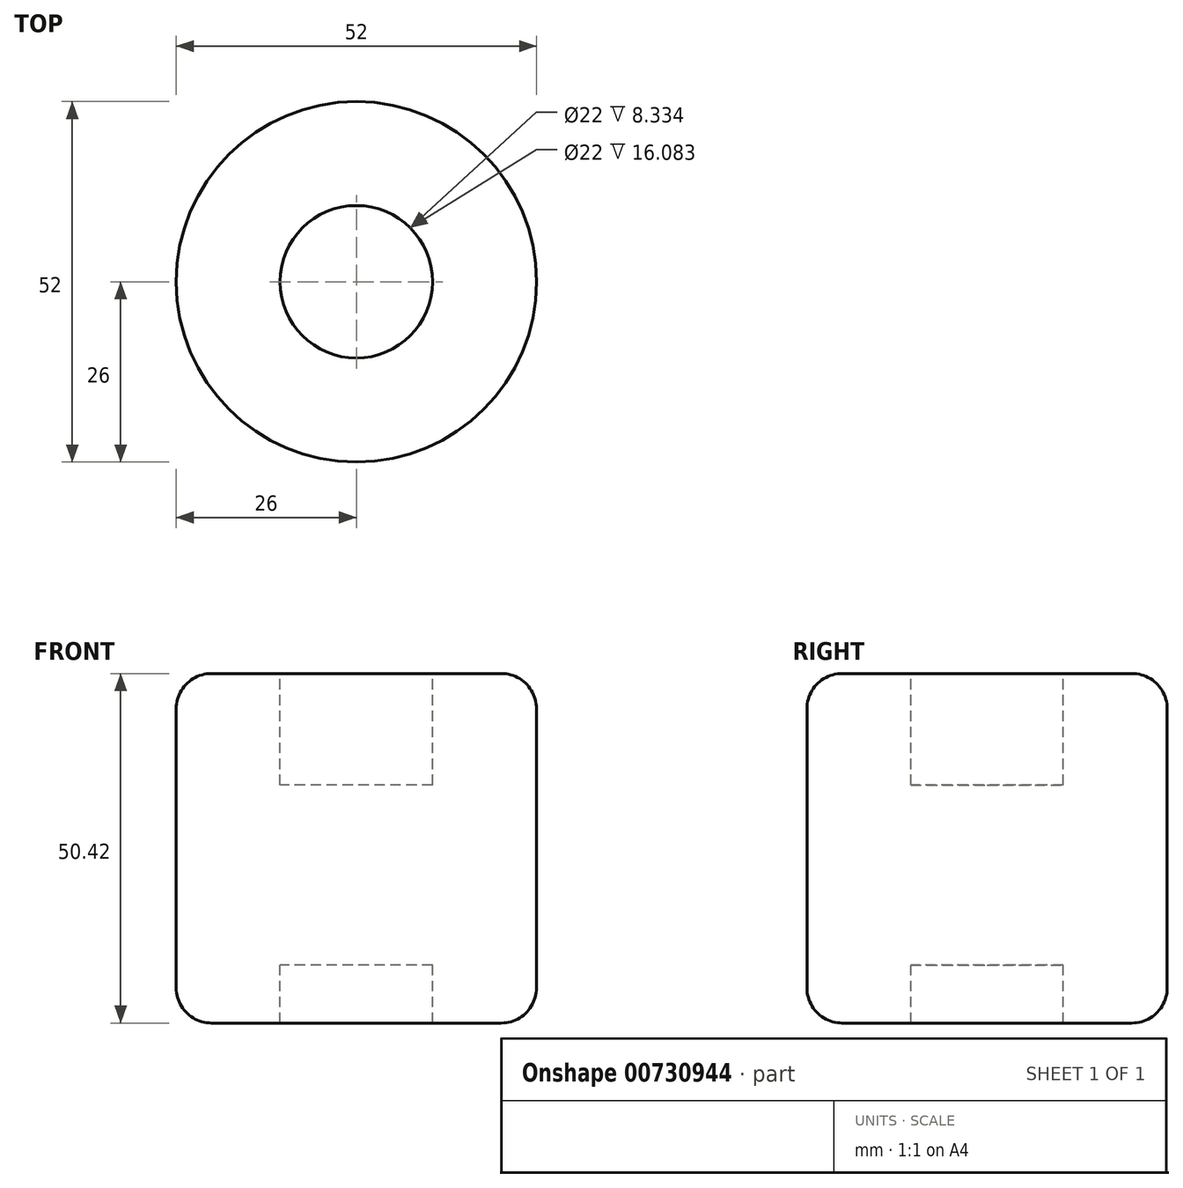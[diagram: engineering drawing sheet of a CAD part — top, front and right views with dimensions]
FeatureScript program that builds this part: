
annotation { "Feature Type Name" : "Feature", "Feature Type Description" : "" }
export const myFeature = defineFeature(function(context is Context, id is Id, definition is map)
    precondition{}
    {
        {
            var Q0;
            Q0=qCreatedBy(makeId("Front.planeOp"),FACE);
            var sketch = newSketch(context, id + "F0", { "sketchPlane" : qUnion([Q0])});
            skLineSegment(sketch, "E0", {"start": v(0, 8.33) * mm, "end": v(11, 8.33) * mm});
            skLineSegment(sketch, "E1", {"start": v(11, 8.33) * mm, "end": v(11, 0) * mm});
            skLineSegment(sketch, "E2", {"start": v(11, 0) * mm, "end": v(26, 0) * mm});
            skLineSegment(sketch, "E3", {"start": v(26, 0) * mm, "end": v(26, 50.42) * mm});
            skLineSegment(sketch, "E4", {"start": v(26, 50.42) * mm, "end": v(11, 50.42) * mm});
            skLineSegment(sketch, "E5", {"start": v(11, 50.42) * mm, "end": v(11, 34.33) * mm});
            skLineSegment(sketch, "E6", {"start": v(11, 34.33) * mm, "end": v(0, 34.33) * mm});
            skLineSegment(sketch, "E7", {"start": v(0, 34.33) * mm, "end": v(0, 8.33) * mm});
            skSolve(sketch);
        }
        {
            var Q0;
            Q0=makeQuery(id+"F0.imprint","IMPRINT",FACE,{"disambiguationData":[TD([[makeQuery(id+"F0.imprint","IMPRINT",EDGE,{"derivedFrom":sQuery(id+"F0.wireOp",EDGE,"E0")}),1.0]])]});
            var Q1;
            Q1=sQuery(id+"F0.wireOp",EDGE,"E7");
            revolve(context, id + "F1", {"surfaceOperationType" : NewSurfaceOperationType.NEW, "entities" : qUnion([Q0]), "axis" : qUnion([Q1]), "revolveType" : RevolveType.FULL});
        }
        {
            var Q0;
            Q0=makeQuery(id+"F1.opRevolve","SWEPT_EDGE",EDGE,{"disambiguationData":[OSD([sQuery(id+"F0.wireOp",EDGE,"E3"),sQuery(id+"F0.wireOp",EDGE,"E4")])]});
            var Q1;
            Q1=makeQuery(id+"F1.opRevolve","SWEPT_EDGE",EDGE,{"disambiguationData":[OSD([sQuery(id+"F0.wireOp",EDGE,"E2"),sQuery(id+"F0.wireOp",EDGE,"E3")])]});
            fillet(context, id + "F2", {"entities" : qUnion([Q0, Q1]), "radius" : 5.08 * mm, "tangentPropagation" : true, "allowEdgeOverflow" : false});
        }
    });
